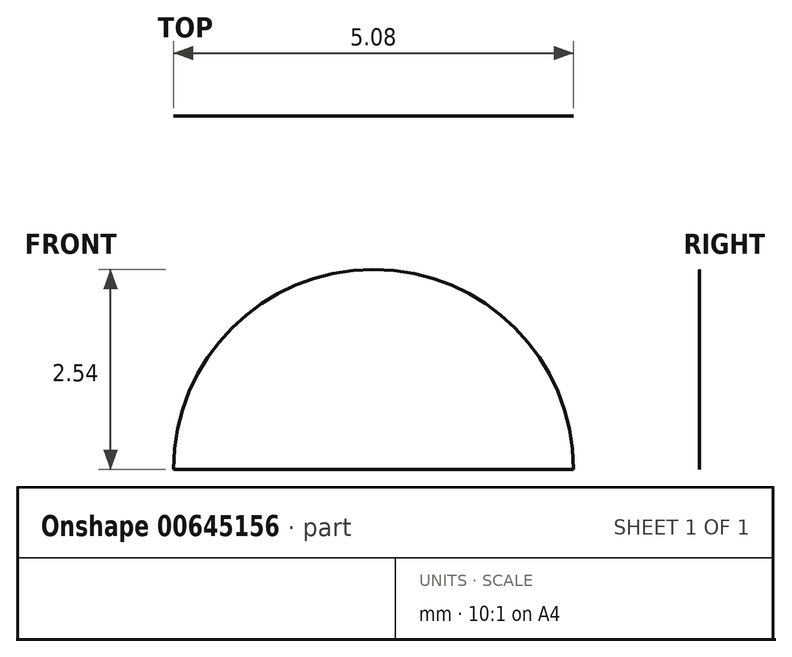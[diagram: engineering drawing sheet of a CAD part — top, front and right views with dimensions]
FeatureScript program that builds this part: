
annotation { "Feature Type Name" : "Feature", "Feature Type Description" : "" }
export const myFeature = defineFeature(function(context is Context, id is Id, definition is map)
    precondition{}
    {
        {
            var Q0;
            Q0=qCreatedBy(makeId("Front.planeOp"),FACE);
            var sketch = newSketch(context, id + "F0", { "sketchPlane" : qUnion([Q0])});
            skLineSegment(sketch, "E0.bottom", {"start": v(76.2, 38.1) * mm, "end": v(-76.2, 38.1) * mm});
            skLineSegment(sketch, "E0.top", {"start": v(76.2, -38.1) * mm, "end": v(-76.2, -38.1) * mm});
            skLineSegment(sketch, "E0.left", {"start": v(76.2, 38.1) * mm, "end": v(76.2, -38.1) * mm});
            skLineSegment(sketch, "E0.right", {"start": v(-76.2, 38.1) * mm, "end": v(-76.2, -38.1) * mm});
            skPoint(sketch, "E0.middle", {"position": v(0, 0) * mm});
            skSolve(sketch);
        }
        {
            var Q0;
            Q0=makeQuery(id+"F0.imprint","IMPRINT",FACE,{"disambiguationData":[TD([[makeQuery(id+"F0.imprint","IMPRINT",EDGE,{"derivedFrom":sQuery(id+"F0.wireOp",EDGE,"E0.bottom")}),1.0]])]});
            extrude(context, id + "F1", {"entities" : qUnion([Q0]), "depth" : 1 / 406.4 * mm, "offsetDistance" : 25.4 * mm});
        }
        {
            var Q0;
            Q0=makeQuery(id+"F1.opExtrude","CAP_FACE",FACE,{"disambiguationData":[OSD([sQuery(id+"F0.wireOp",EDGE,"E0.bottom"),sQuery(id+"F0.wireOp",EDGE,"E0.top"),sQuery(id+"F0.wireOp",EDGE,"E0.left"),sQuery(id+"F0.wireOp",EDGE,"E0.right")])],"isStart":false});
            var sketch = newSketch(context, id + "F2", { "sketchPlane" : qUnion([Q0])});
            skLineSegment(sketch, "E1.bottom", {"start": v(2.54, 25.4) * mm, "end": v(-2.54, 25.4) * mm});
            skLineSegment(sketch, "E1.top", {"start": v(2.54, -25.4) * mm, "end": v(-2.54, -25.4) * mm});
            skLineSegment(sketch, "E1.left", {"start": v(2.54, 25.4) * mm, "end": v(2.54, -25.4) * mm});
            skLineSegment(sketch, "E1.right", {"start": v(-2.54, 25.4) * mm, "end": v(-2.54, -25.4) * mm});
            skPoint(sketch, "E1.middle", {"position": v(0, 0) * mm});
            skSolve(sketch);
        }
        {
            var Q0;
            Q0=makeQuery(id+"F2.imprint","IMPRINT",FACE,{"disambiguationData":[TD([[makeQuery(id+"F2.imprint","IMPRINT",EDGE,{"derivedFrom":sQuery(id+"F2.wireOp",EDGE,"E1.bottom")}),1.0]])]});
            extrude(context, id + "F3", {"entities" : qUnion([Q0]), "operationType" : NewBodyOperationType.REMOVE, "oppositeDirection" : true, "depth" : 25.4 * mm, "offsetDistance" : 25.4 * mm});
        }
        {
            var Q0;
            Q0=makeQuery(id+"F1.opExtrude","CAP_FACE",FACE,{"disambiguationData":[OSD([sQuery(id+"F0.wireOp",EDGE,"E0.bottom"),sQuery(id+"F0.wireOp",EDGE,"E0.top"),sQuery(id+"F0.wireOp",EDGE,"E0.left"),sQuery(id+"F0.wireOp",EDGE,"E0.right")])],"isStart":false});
            var sketch = newSketch(context, id + "F4", { "sketchPlane" : qUnion([Q0])});
            skArc(sketch, "E2", {"start": v(-2.54, 25.4) * mm, "mid": v(0, 27.94) * mm, "end": v(2.54, 25.4) * mm});
            skArc(sketch, "E3", {"start": v(-2.54, -25.4) * mm, "mid": v(0, -27.94) * mm, "end": v(2.54, -25.4) * mm});
            skSolve(sketch);
        }
        {
            var Q0;
            Q0=makeQuery(id+"F4.imprint","IMPRINT",FACE,{"disambiguationData":[TD([[makeQuery(id+"F4.imprint","IMPRINT",EDGE,{"derivedFrom":sQuery(id+"F4.wireOp",EDGE,"E3")}),1.0]])]});
            var Q1;
            Q1=makeQuery(id+"F4.imprint","IMPRINT",FACE,{"disambiguationData":[TD([[makeQuery(id+"F4.imprint","IMPRINT",EDGE,{"derivedFrom":sQuery(id+"F4.wireOp",EDGE,"E2")}),-1.0]])]});
            var Q2;
            Q2=sQuery(id+"F4.wireOp",EDGE,"E2");
            extrude(context, id + "F5", {"entities" : qUnion([Q0, Q1]), "operationType" : NewBodyOperationType.REMOVE, "surfaceEntities" : qUnion([Q2]), "oppositeDirection" : true, "depth" : 25.4 * mm, "offsetDistance" : 25.4 * mm});
        }
    });
